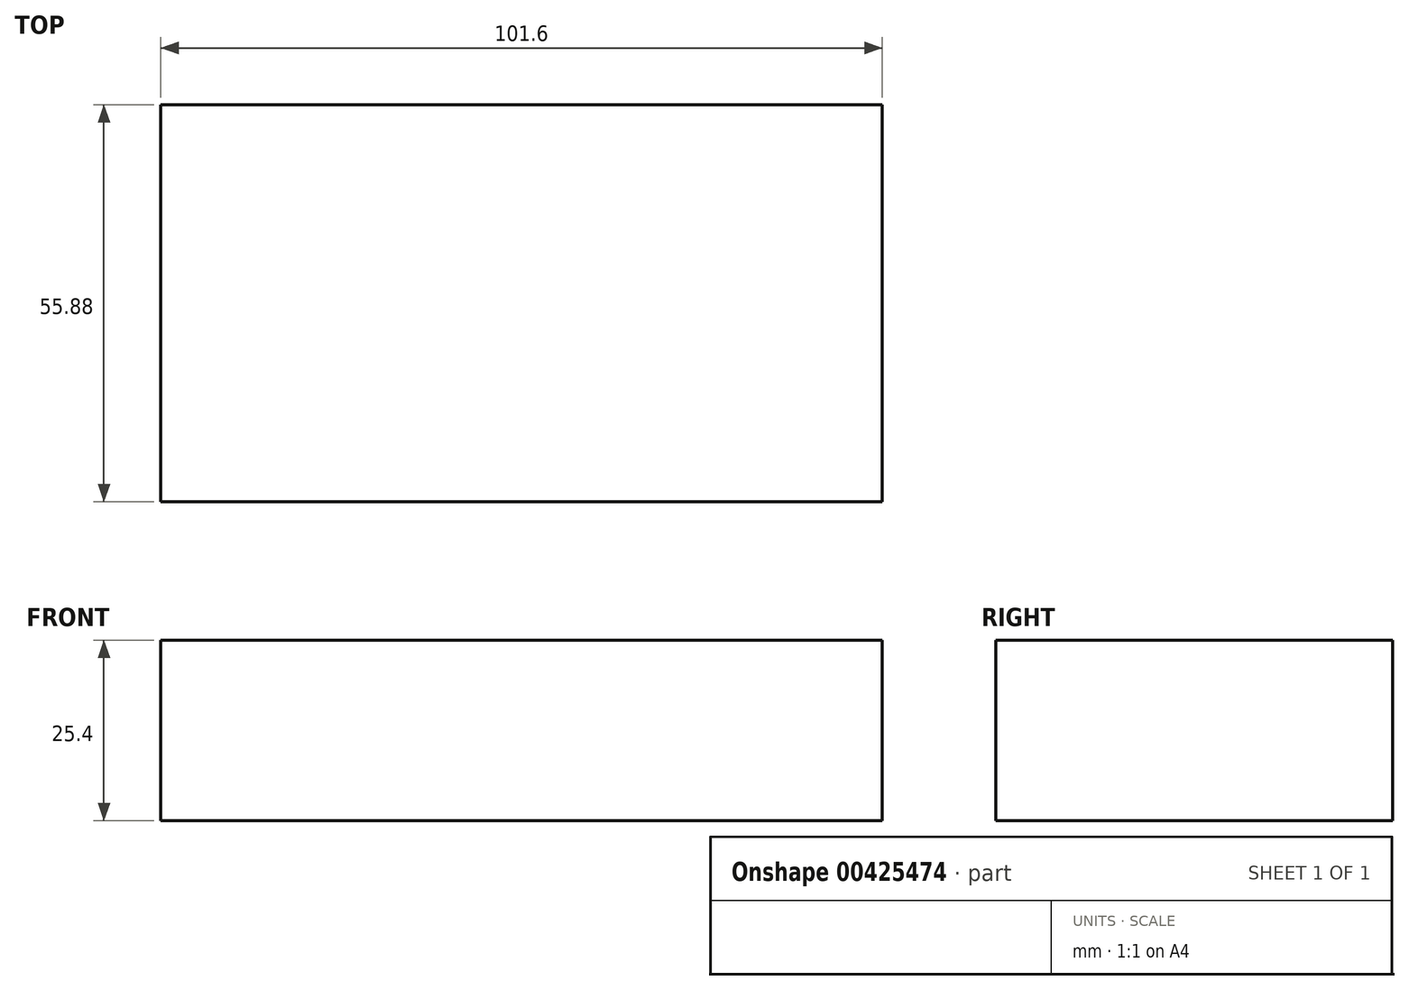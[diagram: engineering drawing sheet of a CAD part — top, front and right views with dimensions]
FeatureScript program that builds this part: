
annotation { "Feature Type Name" : "Feature", "Feature Type Description" : "" }
export const myFeature = defineFeature(function(context is Context, id is Id, definition is map)
    precondition{}
    {
        {
            var Q0;
            Q0=qCreatedBy(makeId("Top.planeOp"),FACE);
            var sketch = newSketch(context, id + "F0", { "sketchPlane" : qUnion([Q0])});
            skLineSegment(sketch, "E0.bottom", {"start": v(50.8, 27.94) * mm, "end": v(-50.8, 27.94) * mm});
            skLineSegment(sketch, "E0.top", {"start": v(50.8, -27.94) * mm, "end": v(-50.8, -27.94) * mm});
            skLineSegment(sketch, "E0.left", {"start": v(50.8, 27.94) * mm, "end": v(50.8, -27.94) * mm});
            skLineSegment(sketch, "E0.right", {"start": v(-50.8, 27.94) * mm, "end": v(-50.8, -27.94) * mm});
            skPoint(sketch, "E0.middle", {"position": v(0, 0) * mm});
            skSolve(sketch);
        }
        {
            var Q0;
            Q0=makeQuery(id+"F0.imprint","IMPRINT",FACE,{"disambiguationData":[TD([[makeQuery(id+"F0.imprint","IMPRINT",EDGE,{"derivedFrom":sQuery(id+"F0.wireOp",EDGE,"E0.bottom")}),1.0]])]});
            extrude(context, id + "F1", {"entities" : qUnion([Q0]), "depth" : 25.4 * mm});
        }
    });
